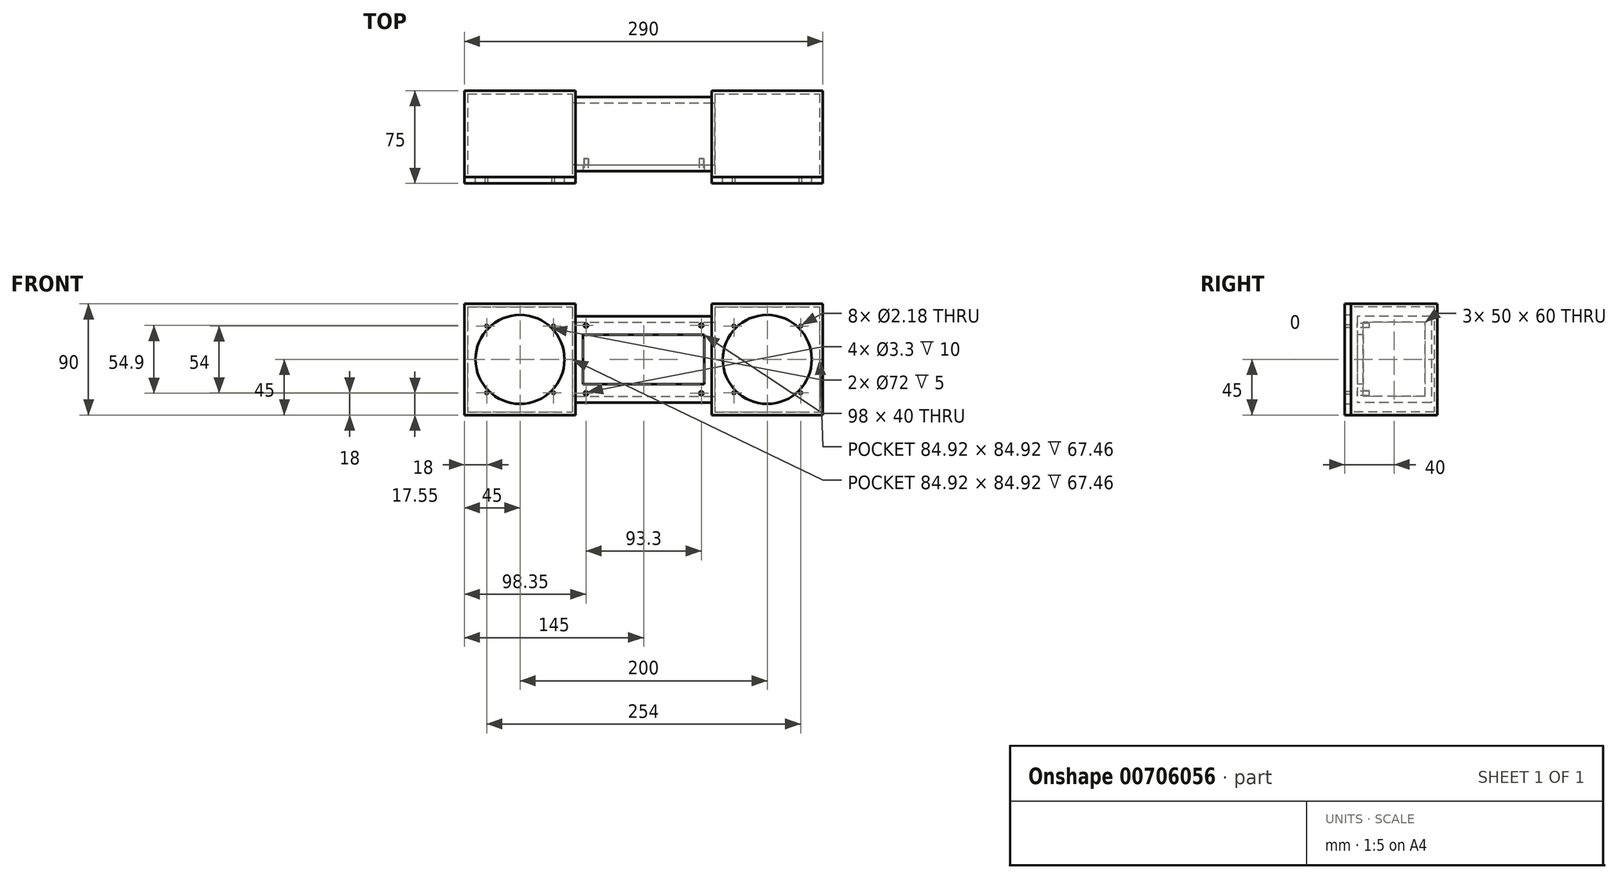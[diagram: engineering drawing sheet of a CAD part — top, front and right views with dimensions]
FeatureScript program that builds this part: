
annotation { "Feature Type Name" : "Feature", "Feature Type Description" : "" }
export const myFeature = defineFeature(function(context is Context, id is Id, definition is map)
    precondition{}
    {
        {
            var Q0;
            Q0=qCreatedBy(makeId("Front.planeOp"),FACE);
            cPlane(context, id + "F0", {"entities" : qUnion([Q0]), "cplaneType" : CPlaneType.OFFSET, "offset" : 30 * mm, "width" : 152.4 * mm, "height" : 152.4 * mm});
        }
        {
            var Q0;
            Q0=qCreatedBy(id+"F0.planeOp",FACE);
            var sketch = newSketch(context, id + "F1", { "sketchPlane" : qUnion([Q0])});
            skLineSegment(sketch, "E0.bottom", {"start": v(-55, 35) * mm, "end": v(55, 35) * mm});
            skLineSegment(sketch, "E0.top", {"start": v(-55, -35) * mm, "end": v(55, -35) * mm});
            skLineSegment(sketch, "E0.left", {"start": v(-55, 35) * mm, "end": v(-55, -35) * mm});
            skLineSegment(sketch, "E0.right", {"start": v(55, 35) * mm, "end": v(55, -35) * mm});
            skPoint(sketch, "E0.middle", {"position": v(0, 0) * mm});
            skSolve(sketch);
        }
        {
            var Q0;
            Q0 = qSketchRegion(id + "F1", true);
            var Q1;
            Q1 = qSketchRegion(id + "F9", true);
            extrude(context, id + "F2", {"entities" : qUnion([Q0, Q1]), "oppositeDirection" : true, "depth" : 60 * mm, "offsetDistance" : 25.4 * mm});
        }
        {
            var Q0;
            Q0=qCreatedBy(makeId("Front.planeOp"),FACE);
            cPlane(context, id + "F3", {"entities" : qUnion([Q0]), "cplaneType" : CPlaneType.OFFSET, "offset" : 35 * mm, "width" : 152.4 * mm, "height" : 152.4 * mm});
        }
        {
            var Q0;
            Q0=qCreatedBy(id+"F3.planeOp",FACE);
            var sketch = newSketch(context, id + "F4", { "sketchPlane" : qUnion([Q0])});
            skLineSegment(sketch, "E1.bottom", {"start": v(-145, 45) * mm, "end": v(-55, 45) * mm});
            skLineSegment(sketch, "E1.top", {"start": v(-145, -45) * mm, "end": v(-55, -45) * mm});
            skLineSegment(sketch, "E1.left", {"start": v(-145, 45) * mm, "end": v(-145, -45) * mm});
            skLineSegment(sketch, "E1.right", {"start": v(-55, 45) * mm, "end": v(-55, -45) * mm});
            skPoint(sketch, "E1.middle", {"position": v(-100, 0) * mm});
            skCircle(sketch, "E2", {"center": v(-100, 0) * mm, "radius": 36 * mm});
            skCircle(sketch, "E3", {"center": v(-127, 27) * mm, "radius": 1.09 * mm});
            skCircle(sketch, "E4", {"center": v(-127, -27) * mm, "radius": 1.09 * mm});
            skCircle(sketch, "E5", {"center": v(-73, 27) * mm, "radius": 1.09 * mm});
            skCircle(sketch, "E6", {"center": v(-73, -27) * mm, "radius": 1.09 * mm});
            skLineSegment(sketch, "E7.bottom", {"start": v(55, 45) * mm, "end": v(145, 45) * mm});
            skLineSegment(sketch, "E7.top", {"start": v(55, -45) * mm, "end": v(145, -45) * mm});
            skLineSegment(sketch, "E7.left", {"start": v(55, 45) * mm, "end": v(55, -45) * mm});
            skLineSegment(sketch, "E7.right", {"start": v(145, 45) * mm, "end": v(145, -45) * mm});
            skPoint(sketch, "E7.middle", {"position": v(100, 0) * mm});
            skCircle(sketch, "E8", {"center": v(100, 0) * mm, "radius": 36 * mm});
            skCircle(sketch, "E9", {"center": v(73, 27) * mm, "radius": 1.09 * mm});
            skCircle(sketch, "E10", {"center": v(73, -27) * mm, "radius": 1.09 * mm});
            skCircle(sketch, "E11", {"center": v(127, 27) * mm, "radius": 1.09 * mm});
            skCircle(sketch, "E12", {"center": v(127, -27) * mm, "radius": 1.09 * mm});
            skSolve(sketch);
        }
        {
            var Q0;
            Q0 = qSketchRegion(id + "F4", true);
            extrude(context, id + "F5", {"entities" : qUnion([Q0]), "depth" : 5 * mm, "offsetDistance" : 25.4 * mm});
        }
        {
            var Q0;
            Q0=qCreatedBy(id+"F3.planeOp",FACE);
            var sketch = newSketch(context, id + "F6", { "sketchPlane" : qUnion([Q0])});
            skLineSegment(sketch, "E13.bottom", {"start": v(-145, 45) * mm, "end": v(-55, 45) * mm});
            skLineSegment(sketch, "E13.top", {"start": v(-145, -45) * mm, "end": v(-55, -45) * mm});
            skLineSegment(sketch, "E13.left", {"start": v(-145, 45) * mm, "end": v(-145, -45) * mm});
            skLineSegment(sketch, "E13.right", {"start": v(-55, 45) * mm, "end": v(-55, -45) * mm});
            skPoint(sketch, "E13.middle", {"position": v(-100, 0) * mm});
            skLineSegment(sketch, "E14.bottom", {"start": v(55, 45) * mm, "end": v(145, 45) * mm});
            skLineSegment(sketch, "E14.top", {"start": v(55, -45) * mm, "end": v(145, -45) * mm});
            skLineSegment(sketch, "E14.left", {"start": v(55, 45) * mm, "end": v(55, -45) * mm});
            skLineSegment(sketch, "E14.right", {"start": v(145, 45) * mm, "end": v(145, -45) * mm});
            skPoint(sketch, "E14.middle", {"position": v(100, 0) * mm});
            skSolve(sketch);
        }
        {
            var Q0;
            Q0 = qSketchRegion(id + "F6", true);
            extrude(context, id + "F7", {"entities" : qUnion([Q0]), "oppositeDirection" : true, "depth" : 70 * mm, "offsetDistance" : 25.4 * mm});
        }
        {
            var Q0;
            Q0=makeQuery(id+"F7.opExtrude","CAP_FACE",FACE,{"disambiguationData":[OSD([sQuery(id+"F6.wireOp",EDGE,"E13.bottom"),sQuery(id+"F6.wireOp",EDGE,"E13.top"),sQuery(id+"F6.wireOp",EDGE,"E13.left"),sQuery(id+"F6.wireOp",EDGE,"E13.right")])],"isStart":true});
            var Q1;
            Q1=makeQuery(id+"F7.opExtrude","CAP_FACE",FACE,{"disambiguationData":[OSD([sQuery(id+"F6.wireOp",EDGE,"E14.bottom"),sQuery(id+"F6.wireOp",EDGE,"E14.top"),sQuery(id+"F6.wireOp",EDGE,"E14.left"),sQuery(id+"F6.wireOp",EDGE,"E14.right")])],"isStart":true});
            shell(context, id + "F8", {"entities" : qUnion([Q0, Q1]), "thickness" : 2.54 * mm});
        }
        {
            var Q0;
            Q0=makeQuery(id+"F2.opExtrude","SWEPT_FACE",FACE,{"disambiguationData":[OSD([sQuery(id+"F1.wireOp",EDGE,"E0.right")])]});
            var sketch = newSketch(context, id + "F9", { "sketchPlane" : qUnion([Q0])});
            skLineSegment(sketch, "E15.bottom", {"start": v(-25, 30) * mm, "end": v(25, 30) * mm});
            skLineSegment(sketch, "E15.top", {"start": v(-25, -30) * mm, "end": v(25, -30) * mm});
            skLineSegment(sketch, "E15.left", {"start": v(-25, 30) * mm, "end": v(-25, -30) * mm});
            skLineSegment(sketch, "E15.right", {"start": v(25, 30) * mm, "end": v(25, -30) * mm});
            skPoint(sketch, "E15.middle", {"position": v(0, 0) * mm});
            skSolve(sketch);
        }
        {
            var Q0;
            Q0 = qSketchRegion(id + "F9", true);
            extrude(context, id + "F10", {"entities" : qUnion([Q0]), "operationType" : NewBodyOperationType.REMOVE, "endBound" : BoundingType.UP_TO_NEXT, "oppositeDirection" : true, "depth" : 25.4 * mm, "offsetDistance" : 25.4 * mm});
        }
        {
            var Q0;
            Q0=makeQuery(id+"F8.opShell","OFFSET_FACE",FACE,{"disambiguationData":[OSD([sQuery(id+"F6.wireOp",EDGE,"E14.left")])]});
            var sketch = newSketch(context, id + "F11", { "sketchPlane" : qUnion([Q0])});
            skLineSegment(sketch, "E16.bottom", {"start": v(-25, 30) * mm, "end": v(25, 30) * mm});
            skLineSegment(sketch, "E16.top", {"start": v(-25, -30) * mm, "end": v(25, -30) * mm});
            skLineSegment(sketch, "E16.left", {"start": v(-25, 30) * mm, "end": v(-25, -30) * mm});
            skLineSegment(sketch, "E16.right", {"start": v(25, 30) * mm, "end": v(25, -30) * mm});
            skPoint(sketch, "E16.middle", {"position": v(0, 0) * mm});
            skSolve(sketch);
        }
        {
            var Q0;
            Q0 = qSketchRegion(id + "F11", true);
            extrude(context, id + "F12", {"entities" : qUnion([Q0]), "operationType" : NewBodyOperationType.REMOVE, "oppositeDirection" : true, "depth" : 25.4 * mm, "offsetDistance" : 25.4 * mm});
        }
        {
            var Q0;
            Q0=makeQuery(id+"F8.opShell","OFFSET_FACE",FACE,{"disambiguationData":[OSD([sQuery(id+"F6.wireOp",EDGE,"E13.right")])]});
            var sketch = newSketch(context, id + "F13", { "sketchPlane" : qUnion([Q0])});
            skLineSegment(sketch, "E17.bottom", {"start": v(-25, 30) * mm, "end": v(25, 30) * mm});
            skLineSegment(sketch, "E17.top", {"start": v(-25, -30) * mm, "end": v(25, -30) * mm});
            skLineSegment(sketch, "E17.left", {"start": v(-25, 30) * mm, "end": v(-25, -30) * mm});
            skLineSegment(sketch, "E17.right", {"start": v(25, 30) * mm, "end": v(25, -30) * mm});
            skPoint(sketch, "E17.middle", {"position": v(0, 0) * mm});
            skSolve(sketch);
        }
        {
            var Q0;
            Q0 = qSketchRegion(id + "F13", true);
            extrude(context, id + "F14", {"entities" : qUnion([Q0]), "operationType" : NewBodyOperationType.REMOVE, "oppositeDirection" : true, "depth" : 25.4 * mm, "offsetDistance" : 25.4 * mm});
        }
        {
            var Q0;
            Q0=qCreatedBy(id+"F0.planeOp",FACE);
            var sketch = newSketch(context, id + "F15", { "sketchPlane" : qUnion([Q0])});
            skLineSegment(sketch, "E18.bottom", {"start": v(-49, 20) * mm, "end": v(49, 20) * mm});
            skLineSegment(sketch, "E18.top", {"start": v(-49, -20) * mm, "end": v(49, -20) * mm});
            skLineSegment(sketch, "E18.left", {"start": v(-49, 20) * mm, "end": v(-49, -20) * mm});
            skLineSegment(sketch, "E18.right", {"start": v(49, 20) * mm, "end": v(49, -20) * mm});
            skPoint(sketch, "E18.middle", {"position": v(0, 0) * mm});
            skCircle(sketch, "E19", {"center": v(46.65, 27.45) * mm, "radius": 1.65 * mm});
            skCircle(sketch, "E20", {"center": v(-46.65, 27.45) * mm, "radius": 1.65 * mm});
            skCircle(sketch, "E21", {"center": v(-46.65, -27.45) * mm, "radius": 1.65 * mm});
            skCircle(sketch, "E22", {"center": v(46.65, -27.45) * mm, "radius": 1.65 * mm});
            skSolve(sketch);
        }
        {
            var Q0;
            Q0 = qSketchRegion(id + "F15", true);
            extrude(context, id + "F16", {"entities" : qUnion([Q0]), "operationType" : NewBodyOperationType.REMOVE, "oppositeDirection" : true, "depth" : 25.4 * mm, "offsetDistance" : 25.4 * mm});
        }
        {
            var Q0;
            Q0=makeQuery(id+"F10.boolean.opBoolean","COPY",FACE,{"derivedFrom":makeQuery(id+"F10.opExtrude","SWEPT_FACE",FACE,{"disambiguationData":[OSD([sQuery(id+"F9.wireOp",EDGE,"E15.left")])]})});
            var sketch = newSketch(context, id + "F17", { "sketchPlane" : qUnion([Q0])});
            skCircle(sketch, "E23", {"center": v(-46.65, 27.45) * mm, "radius": 1.65 * mm});
            skCircle(sketch, "E24", {"center": v(-46.65, 27.45) * mm, "radius": 1.9 * mm});
            skCircle(sketch, "E25", {"center": v(46.65, 27.45) * mm, "radius": 1.65 * mm});
            skCircle(sketch, "E26", {"center": v(46.65, 27.45) * mm, "radius": 1.9 * mm});
            skCircle(sketch, "E27", {"center": v(46.65, -27.45) * mm, "radius": 1.65 * mm});
            skCircle(sketch, "E28", {"center": v(46.65, -27.45) * mm, "radius": 1.9 * mm});
            skCircle(sketch, "E29", {"center": v(-46.65, -27.45) * mm, "radius": 1.65 * mm});
            skCircle(sketch, "E30", {"center": v(-46.65, -27.45) * mm, "radius": 1.9 * mm});
            skSolve(sketch);
        }
        {
            var Q0;
            Q0 = qSketchRegion(id + "F17", true);
            extrude(context, id + "F18", {"entities" : qUnion([Q0]), "operationType" : NewBodyOperationType.ADD, "depth" : 5 * mm, "offsetDistance" : 25.4 * mm});
        }
    });
